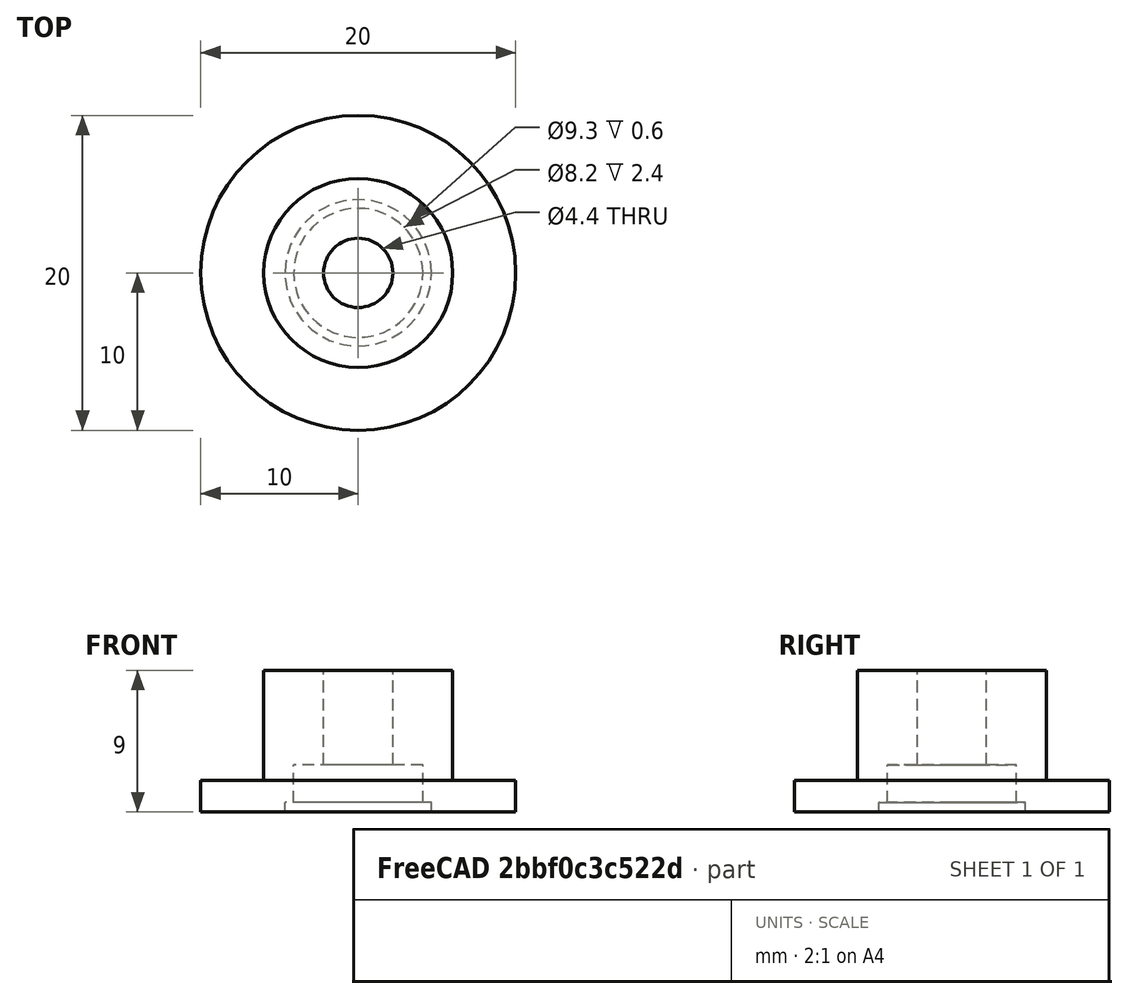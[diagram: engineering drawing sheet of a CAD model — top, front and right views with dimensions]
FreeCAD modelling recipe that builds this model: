
FCSTD DOCUMENT  (FreeCAD 0.19R24276 (Git))
Label: Art3TensionerPulley
License: All rights reserved
LicenseURL: http://en.wikipedia.org/wiki/All_rights_reserved
objects: PartDesign::CoordinateSystem×2, Sketcher::SketchObject×1, PartDesign::Revolution×1, PartDesign::Body×1
note: 6 computed .brp shape members not serialized (recipe doc carries the construction recipe); baked Part::Feature solids carry a one-line shape summary decoded from their .brp

FEATURE [Sketcher::SketchObject] Sketch
  FullyConstrained = true
  MapMode = 5
  Placement = pos=(0,0,0) rot=(1,0,0;1.5708rad)
  Support = -> [XZ_Plane]
  sketch-geometry (10):
    g0: LineSegment StartX=2.2 StartY=9 StartZ=0 EndX=6 EndY=9 EndZ=0
    g1: LineSegment StartX=6 StartY=9 StartZ=0 EndX=6 EndY=2 EndZ=0
    g2: LineSegment StartX=6 StartY=2 StartZ=0 EndX=10 EndY=2 EndZ=0
    g3: LineSegment StartX=10 StartY=2 StartZ=0 EndX=10 EndY=0 EndZ=0
    g4: LineSegment StartX=10 StartY=0 StartZ=0 EndX=4.65 EndY=0 EndZ=0
    g5: LineSegment StartX=4.65 StartY=0 StartZ=0 EndX=4.65 EndY=0.6 EndZ=0
    g6: LineSegment StartX=4.65 StartY=0.6 StartZ=0 EndX=4.1 EndY=0.6 EndZ=0
    g7: LineSegment StartX=4.1 StartY=0.6 StartZ=0 EndX=4.1 EndY=3 EndZ=0
    g8: LineSegment StartX=4.1 StartY=3 StartZ=0 EndX=2.2 EndY=3 EndZ=0
    g9: LineSegment StartX=2.2 StartY=3 StartZ=0 EndX=2.2 EndY=9 EndZ=0
  constraints (30):
    c: Horizontal(g0)
    c: Coincident(g0,g1)
    c: Vertical(g1)
    c: Coincident(g1,g2)
    c: Horizontal(g2)
    c: Coincident(g2,g3)
    c: Vertical(g3)
    c: Coincident(g3,g4)
    c: Horizontal(g4)
    c: Coincident(g4,g5)
    c: Vertical(g5)
    c: Coincident(g5,g6)
    c: Coincident(g6,g7)
    c: Vertical(g7)
    c: Coincident(g7,g8)
    c: Horizontal(g8)
    c: Coincident(g8,g9)
    c: Coincident(g9,g0)
    c: Vertical(g9)
    c: Horizontal(g6)
    c: DistanceX(g-1,g8) = 2.2
    c: DistanceX(g-1,g6) = 4.1
    c: DistanceX(g-1,g4) = 4.65
    c: DistanceX(g-1,g0) = 6
    c: DistanceX(g-1,g3) = 10
    c: PointOnObject(g4,g-1)
    c: DistanceY(g5,g5) = 0.6
    c: DistanceY(g-1,g7) = 3
    c: DistanceY(g-1,g0) = 9
    c: DistanceY(g3,g3) = 2
FEATURE [PartDesign::Revolution] Revolution
  Angle = 360
  Axis = (0,2e-16,1)
  Base = (0,0,0)
  Placement = pos=(0,0,0) rot=(1,0,0;1.5708rad)
  Profile = -> Sketch
  ReferenceAxis = -> Sketch [V_Axis]
  Refine = true
  Reversed = true
FEATURE [PartDesign::CoordinateSystem] LCS_Art3TensionerPulley
  AttacherType = Attacher::AttachEngine3D
  MapMode = 11
  Placement = pos=(-4e-16,6e-15,9) rot=(0.707107,-0.707107,0;3.14159rad)
  Support = -> [Revolution]
FEATURE [PartDesign::CoordinateSystem] LCS_Bearing
  AttacherType = Attacher::AttachEngine3D
  MapMode = 11
  Placement = pos=(0,0,0) rot=(0.707107,-0.707107,0;3.14159rad)
  Support = -> [Revolution]
FEATURE [PartDesign::Body] Body  label="Art3TensionerPulley"
  Group = -> [Sketch,Revolution,LCS_Art3TensionerPulley,LCS_Bearing]
  Origin = -> Origin
  Tip = -> Revolution
